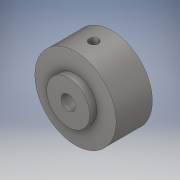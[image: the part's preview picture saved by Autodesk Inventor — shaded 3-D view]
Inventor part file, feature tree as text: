
AUTODESK INVENTOR PART (.ipt)
format: ipt  version: 2018 (Build 220112000, 112)  size: 125,952 bytes
history: native  units: in
note: dims shown in document units (in); Inventor stores cm internally (conversion verified against a paired STEP export)
features: extrude x4, sketch x4
ambient origin geometry x8: Origin, YZ Plane, XZ Plane, XY Plane, X Axis, Y Axis, Z Axis, Center Point
bodies: Solid1 (feature_tree)
feature tree (8):
  extrude  "Extrusion1"  Depth=0.625in TaperAngle=0.0deg
  extrude  "Extrusion2"  Depth=0.125in TaperAngle=0.0deg
  extrude  "Extrusion3"  Depth=1.0in TaperAngle=0.0deg
  extrude  "Extrusion4"  Depth=0.3125in TaperAngle=0.0deg
  sketch  "Sketch1"  dims[d0=1.4in d2=0.625in d3=0.0in]
  sketch  "Sketch2"  dims[d4=0.74in d5=0.125in d6=0.0in]
  sketch  "Sketch3"  dims[d7=0.25in d8=1.0in d9=0.0in]
  sketch  "Sketch4"  dims[d10=0.159in d11=1.0in d12=0.0in d13=0.3125in]
